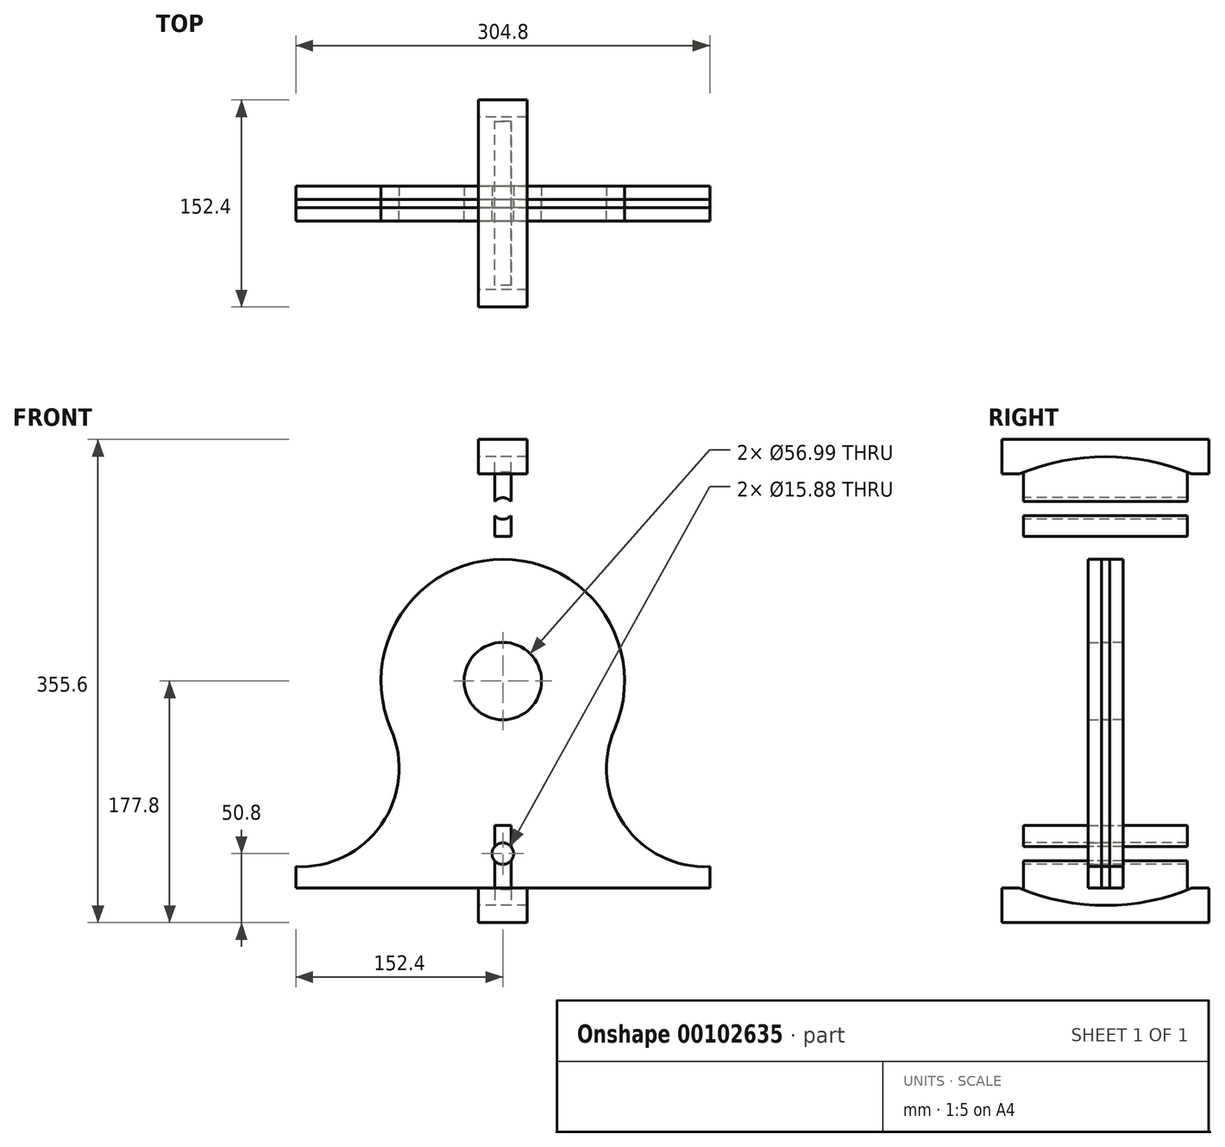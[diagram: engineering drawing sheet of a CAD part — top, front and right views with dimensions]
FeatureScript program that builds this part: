
annotation { "Feature Type Name" : "Feature", "Feature Type Description" : "" }
export const myFeature = defineFeature(function(context is Context, id is Id, definition is map)
    precondition{}
    {
        {
            assignVariable(context, id + "F0", {"name" : "Dpth", "anyValue" : 6});
        }
        {
            assignVariable(context, id + "F1", {"name" : "ChannelLnth", "anyValue" : 36});
        }
        {
            var Q0;
            Q0=qCreatedBy(makeId("Right.planeOp"),FACE);
            var sketch = newSketch(context, id + "F2", { "sketchPlane" : qUnion([Q0])});
            skLineSegment(sketch, "E0.bottom", {"start": v(-76.2, -177.8) * mm, "end": v(76.2, -177.8) * mm});
            skLineSegment(sketch, "E0.top", {"start": v(-76.2, -152.4) * mm, "end": v(76.2, -152.4) * mm});
            skLineSegment(sketch, "E0.left", {"start": v(-76.2, -177.8) * mm, "end": v(-76.2, -152.4) * mm});
            skLineSegment(sketch, "E0.right", {"start": v(76.2, -177.8) * mm, "end": v(76.2, -152.4) * mm});
            skLineSegment(sketch, "E1", {"start": v(0, -152.4) * mm, "end": v(0, -177.8) * mm, "construction": true});
            skArc(sketch, "E2", {"start": v(-63.5, -152.4) * mm, "mid": v(0, -165.1) * mm, "end": v(63.5, -152.4) * mm});
            skSolve(sketch);
        }
        {
            var Q0;
            Q0=makeQuery(id+"F2.imprint","IMPRINT",FACE,{"disambiguationData":[TD([[makeQuery(id+"F2.imprint","IMPRINT",EDGE,{"derivedFrom":sQuery(id+"F2.wireOp",EDGE,"E0.bottom")}),1.0]])]});
            extrude(context, id + "F3", {"entities" : qUnion([Q0]), "endBound" : BoundingType.SYMMETRIC, "depth" : (getVariable(context, 'ChannelLnth')) * mm});
        }
        {
            var Q0;
            Q0=qCreatedBy(makeId("Front.planeOp"),FACE);
            cPlane(context, id + "F4", {"entities" : qUnion([Q0]), "cplaneType" : CPlaneType.OFFSET, "offset" : (getVariable(context, 'Dpth') / 2) * mm, "width" : 152.4 * mm, "height" : 152.4 * mm});
        }
        {
            var Q0;
            Q0=qCreatedBy(id+"F4.planeOp",FACE);
            var sketch = newSketch(context, id + "F5", { "sketchPlane" : qUnion([Q0])});
            skCircle(sketch, "E3", {"center": v(0, 0) * mm, "radius": 89.62 * mm});
            skLineSegment(sketch, "E4", {"start": v(0, -152.4) * mm, "end": v(152.4, -152.4) * mm});
            skLineSegment(sketch, "E5", {"start": v(152.4, -152.4) * mm, "end": v(152.4, -136.53) * mm});
            skArc(sketch, "E6", {"start": v(82.28, -35.53) * mm, "mid": v(89.27, -105.51) * mm, "end": v(152.4, -136.53) * mm});
            skLineSegment(sketch, "E7", {"start": v(-33.02, 0) * mm, "end": v(47.42, 0) * mm, "construction": true});
            skArc(sketch, "E8.MirrorCS", {"start": v(82.28, 35.53) * mm, "mid": v(89.27, 105.51) * mm, "end": v(152.4, 136.53) * mm});
            skLineSegment(sketch, "E9.MirrorCS", {"start": v(152.4, 152.4) * mm, "end": v(152.4, 136.53) * mm});
            skLineSegment(sketch, "E10.MirrorCS", {"start": v(0, 152.4) * mm, "end": v(152.4, 152.4) * mm});
            skLineSegment(sketch, "E11", {"start": v(0, -36.12) * mm, "end": v(0, 41.06) * mm, "construction": true});
            skLineSegment(sketch, "E12.MirrorCS", {"start": v(0, 152.4) * mm, "end": v(-152.4, 152.4) * mm});
            skLineSegment(sketch, "E13.MirrorCS", {"start": v(-152.4, 152.4) * mm, "end": v(-152.4, 136.53) * mm});
            skArc(sketch, "E14.MirrorCS", {"start": v(-82.28, 35.53) * mm, "mid": v(-89.27, 105.51) * mm, "end": v(-152.4, 136.53) * mm});
            skArc(sketch, "E15.MirrorCS", {"start": v(-82.28, -35.53) * mm, "mid": v(-89.27, -105.51) * mm, "end": v(-152.4, -136.53) * mm});
            skLineSegment(sketch, "E16.MirrorCS", {"start": v(-152.4, -152.4) * mm, "end": v(-152.4, -136.53) * mm});
            skLineSegment(sketch, "E17.MirrorCS", {"start": v(0, -152.4) * mm, "end": v(-152.4, -152.4) * mm});
            skCircle(sketch, "E18", {"center": v(0, -127) * mm, "radius": 7.94 * mm});
            skCircle(sketch, "E19.MirrorC", {"center": v(0, 127) * mm, "radius": 7.94 * mm});
            skCircle(sketch, "E20", {"center": v(0, 0) * mm, "radius": 28.5 * mm});
            skSolve(sketch);
        }
        {
            var Q0;
            {var subQ0=sQuery(id+"F5.wireOp",EDGE,"E8.MirrorCS");Q0=makeQuery(id+"F5.imprint","IMPRINT",FACE,{"disambiguationData":[TD([[makeQuery(id+"F5.imprint","IMPRINT",EDGE,{"derivedFrom":subQ0}),1.0]])]});}
            var Q1;
            {var subQ0=sQuery(id+"F5.wireOp",EDGE,"E3");var subQ1=makeQuery(id+"F5.imprint","INTERSECT",VERTEX,{"derivedFrom":[subQ0,sQuery(id+"F5.wireOp",EDGE,"E8.MirrorCS")]});Q1=makeQuery(id+"F5.imprint","IMPRINT",FACE,{"disambiguationData":[TD([[makeQuery(id+"F5.imprint","IMPRINT",EDGE,{"disambiguationData":[TD([[subQ1,-1.0]])],"derivedFrom":subQ0}),1.0]])]});}
            var Q2;
            Q2=makeQuery(id+"F5.imprint","IMPRINT",FACE,{"disambiguationData":[TD([[makeQuery(id+"F5.imprint","IMPRINT",EDGE,{"derivedFrom":sQuery(id+"F5.wireOp",EDGE,"E4")}),1.0]])]});
            extrude(context, id + "F6", {"entities" : qUnion([Q0, Q1, Q2]), "oppositeDirection" : true, "depth" : 15.88 * mm});
        }
        {
            var Q0;
            Q0=qCreatedBy(makeId("Right.planeOp"),FACE);
            var sketch = newSketch(context, id + "F7", { "sketchPlane" : qUnion([Q0])});
            skArc(sketch, "E21.0", {"start": v(-63.5, -152.4) * mm, "mid": v(0, -165.1) * mm, "end": v(63.5, -152.4) * mm});
            skLineSegment(sketch, "E22", {"start": v(0, 31.76) * mm, "end": v(0, -53.99) * mm, "construction": true});
            skLineSegment(sketch, "E23", {"start": v(-60.32, -106.34) * mm, "end": v(-60.32, -153.68) * mm});
            skLineSegment(sketch, "E24.MirrorCS", {"start": v(60.32, -106.34) * mm, "end": v(60.32, -153.68) * mm});
            skLineSegment(sketch, "E25", {"start": v(-60.32, -106.34) * mm, "end": v(60.32, -106.34) * mm});
            skSolve(sketch);
        }
        {
            var Q0;
            Q0 = qSketchRegion(id + "F7", true);
            extrude(context, id + "F8", {"entities" : qUnion([Q0]), "endBound" : BoundingType.SYMMETRIC, "depth" : (getVariable(context, 'Dpth') * 2) * mm});
        }
        {
            var Q0;
            Q0=makeQuery(id+"F8.opExtrude","SWEPT_FACE",FACE,{"disambiguationData":[OSD([sQuery(id+"F7.wireOp",EDGE,"E23")])]});
            var sketch = newSketch(context, id + "F9", { "sketchPlane" : qUnion([Q0])});
            skArc(sketch, "E26.0", {"start": v(82.28, -35.53) * mm, "mid": v(123.2, -131.96) * mm, "end": v(217.6, -86.55) * mm});
            skPoint(sketch, "E27.orphan", {"position": v(152.4, -136.52) * mm});
            skLineSegment(sketch, "E28", {"start": v(82.28, -35.53) * mm, "end": v(217.6, -86.55) * mm});
            skCircle(sketch, "E29.0", {"center": v(0, -127) * mm, "radius": 7.94 * mm});
            skLineSegment(sketch, "E30", {"start": v(0, 0) * mm, "end": v(0, -36.51) * mm, "construction": true});
            skArc(sketch, "E31.MirrorCS", {"start": v(-82.28, -35.53) * mm, "mid": v(-123.2, -131.96) * mm, "end": v(-217.6, -86.55) * mm});
            skLineSegment(sketch, "E32.MirrorCS", {"start": v(-82.28, -35.53) * mm, "end": v(-217.6, -86.55) * mm});
            skSolve(sketch);
        }
        {
            var Q0;
            Q0 = qSketchRegion(id + "F9", true);
            extrude(context, id + "F10", {"entities" : qUnion([Q0]), "operationType" : NewBodyOperationType.REMOVE, "endBound" : BoundingType.THROUGH_ALL, "oppositeDirection" : true, "depth" : 25.4 * mm});
        }
        {
            var Q0;
            Q0=makeQuery(id+"F3.opExtrude","SWEPT_BODY",BODY,{"disambiguationData":[OSD([sQuery(id+"F2.wireOp",EDGE,"E0.bottom"),sQuery(id+"F2.wireOp",EDGE,"E0.top"),sQuery(id+"F2.wireOp",EDGE,"E0.left"),sQuery(id+"F2.wireOp",EDGE,"E0.right"),sQuery(id+"F2.wireOp",EDGE,"E2")])]});
            var Q1;
            Q1=makeQuery(id+"F8.opExtrude","SWEPT_BODY",BODY,{"disambiguationData":[OSD([sQuery(id+"F7.wireOp",EDGE,"E21.0"),sQuery(id+"F7.wireOp",EDGE,"E23"),sQuery(id+"F7.wireOp",EDGE,"E24.MirrorCS"),sQuery(id+"F7.wireOp",EDGE,"E25")])]});
            var Q2;
            Q2=qCreatedBy(makeId("Top.planeOp"),FACE);
            mirror(context, id + "F11", {"entities" : qUnion([Q0, Q1]), "mirrorPlane" : qUnion([Q2])});
        }
        {
            var Q0;
            Q0=makeQuery(id+"F6.opExtrude","SWEPT_BODY",BODY,{"disambiguationData":[OSD([sQuery(id+"F5.wireOp",EDGE,"E3"),sQuery(id+"F5.wireOp",EDGE,"E4"),sQuery(id+"F5.wireOp",EDGE,"E5"),sQuery(id+"F5.wireOp",EDGE,"E6"),sQuery(id+"F5.wireOp",EDGE,"E8.MirrorCS"),sQuery(id+"F5.wireOp",EDGE,"E9.MirrorCS"),sQuery(id+"F5.wireOp",EDGE,"E10.MirrorCS"),sQuery(id+"F5.wireOp",EDGE,"E12.MirrorCS"),sQuery(id+"F5.wireOp",EDGE,"E13.MirrorCS"),sQuery(id+"F5.wireOp",EDGE,"E14.MirrorCS"),sQuery(id+"F5.wireOp",EDGE,"E15.MirrorCS"),sQuery(id+"F5.wireOp",EDGE,"E16.MirrorCS"),sQuery(id+"F5.wireOp",EDGE,"E17.MirrorCS"),sQuery(id+"F5.wireOp",EDGE,"E18"),sQuery(id+"F5.wireOp",EDGE,"E19.MirrorC")])]});
            var Q1;
            Q1=qCreatedBy(makeId("Front.planeOp"),FACE);
            mirror(context, id + "F12", {"entities" : qUnion([Q0]), "mirrorPlane" : qUnion([Q1])});
        }
    });
